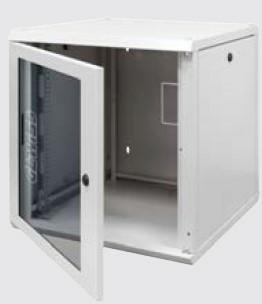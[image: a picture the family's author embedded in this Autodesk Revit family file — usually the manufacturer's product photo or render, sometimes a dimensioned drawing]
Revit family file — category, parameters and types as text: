
# Revit family: Domotics-NetworkCabling-GEWISS-CABINETS_WALL-MOUNTED_19_12U_D400
name_source: partatom
category: Apparecchi elettrici
units: mm (PartAtom-declared; Revit-internal decimal feet)

## family parameters
Condiviso = No
Host = Superficie
Mantenere orientamento annotazione = Sì
Punto di calcolo locali = Sì
Quota connettore circolare = Usa diametro
Taglio con vuoti quando caricato = No
Tipo di parte = Normale

## types (1)
- GW38408 - WALL CABINET 19 12U DEPTH 400MM.
    Cabling unity = 12 U
    Catalogue = DOMOTICS
    Category = 19â€ wall-mount cabinet
    Colour = Grey (RAL 7035)
    Depth (mm) = 400 mm
    Descrizione = WALL CABINET 19 12U DEPTH 400MM.
    Door opening = 180°
    Electrocod = 3752
    Finishing = Textured
    IDF = 1b5b25df-0790-44a8-97b3-88640d171cf5
    IDT = 601a335b6a224bb6a86d85924b08be06
    IP degree = IP20
    Immagine tipo = B.jpg
    Material = Steel
    Modello = GW38408
    N_poli = 1
    No. uprights = 2
    Outer dim. LxHxD (mm) = 600x605x400
    Potenza quadro = 0 V
    Produttore = GEWISS S.p.A.
    Prospetto di default = 1219 mm
    SEO = Board
    Static load capacity = 50KG
    Technical sheet = https://www.gewiss.com
    Type of door = Reversible
    URL = https://www.gewiss.com
    Version file RFA = 21.2

## geometry (parser evidence)
native form markers: Sweep x4
no freeform markers — native parametric forms only
